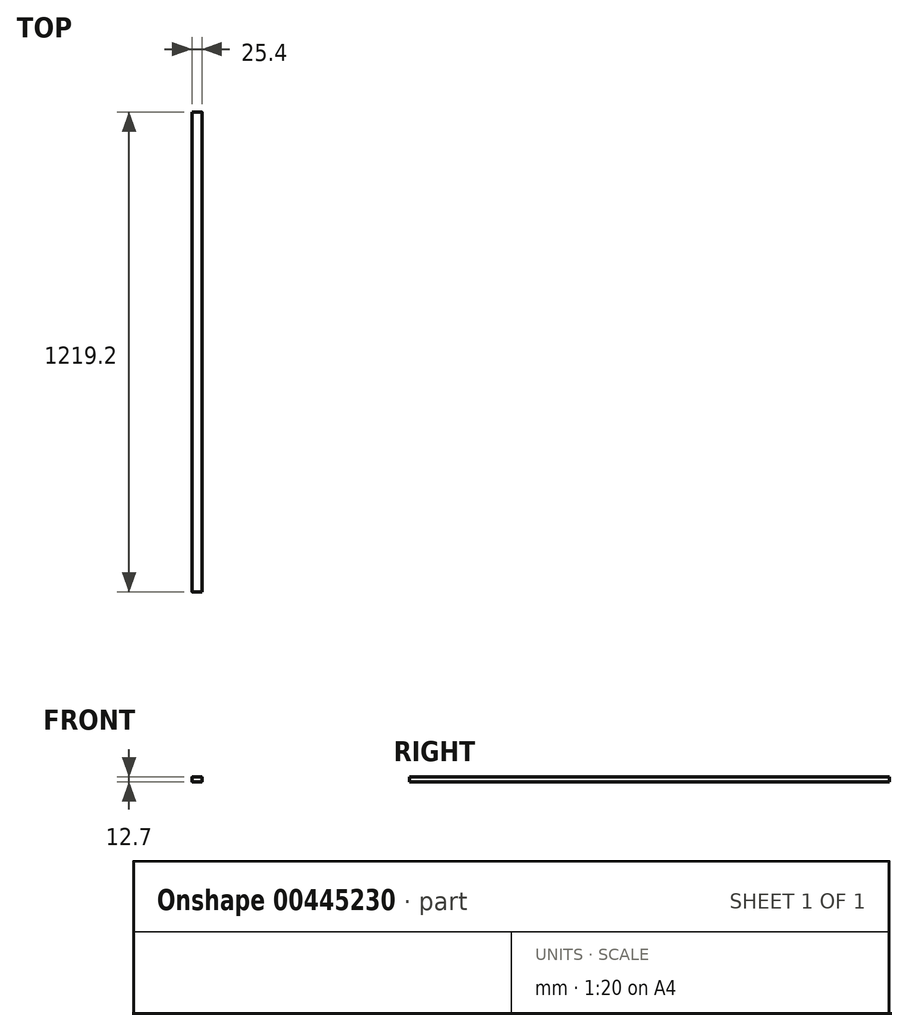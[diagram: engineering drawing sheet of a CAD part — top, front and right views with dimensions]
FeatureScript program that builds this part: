
annotation { "Feature Type Name" : "Feature", "Feature Type Description" : "" }
export const myFeature = defineFeature(function(context is Context, id is Id, definition is map)
    precondition{}
    {
        {
            var Q0;
            Q0=qCreatedBy(makeId("Front.planeOp"),FACE);
            var sketch = newSketch(context, id + "F0", { "sketchPlane" : qUnion([Q0])});
            skLineSegment(sketch, "E0.bottom", {"start": v(-12.7, 6.35) * mm, "end": v(12.7, 6.35) * mm});
            skLineSegment(sketch, "E0.top", {"start": v(-12.7, -6.35) * mm, "end": v(12.7, -6.35) * mm});
            skLineSegment(sketch, "E0.left", {"start": v(-12.7, 6.35) * mm, "end": v(-12.7, -6.35) * mm});
            skLineSegment(sketch, "E0.right", {"start": v(12.7, 6.35) * mm, "end": v(12.7, -6.35) * mm});
            skPoint(sketch, "E0.middle", {"position": v(0, 0) * mm});
            skSolve(sketch);
        }
        {
            var Q0;
            Q0 = qSketchRegion(id + "F0", true);
            extrude(context, id + "F1", {"entities" : qUnion([Q0]), "oppositeDirection" : true, "depth" : 1219.2 * mm});
        }
        {
            var Q0;
            Q0=makeQuery(id+"F1.opExtrude","SWEPT_EDGE",EDGE,{"disambiguationData":[OSD([sQuery(id+"F0.wireOp",EDGE,"E0.bottom"),sQuery(id+"F0.wireOp",EDGE,"E0.right")])]});
            var Q1;
            Q1=makeQuery(id+"F1.opExtrude","SWEPT_EDGE",EDGE,{"disambiguationData":[OSD([sQuery(id+"F0.wireOp",EDGE,"E0.bottom"),sQuery(id+"F0.wireOp",EDGE,"E0.left")])]});
            var Q2;
            Q2=makeQuery(id+"F1.opExtrude","SWEPT_EDGE",EDGE,{"disambiguationData":[OSD([sQuery(id+"F0.wireOp",EDGE,"E0.top"),sQuery(id+"F0.wireOp",EDGE,"E0.right")])]});
            var Q3;
            Q3=makeQuery(id+"F1.opExtrude","SWEPT_EDGE",EDGE,{"disambiguationData":[OSD([sQuery(id+"F0.wireOp",EDGE,"E0.top"),sQuery(id+"F0.wireOp",EDGE,"E0.left")])]});
            fillet(context, id + "F2", {"entities" : qUnion([Q0, Q1, Q2, Q3]), "radius" : 1 * mm, "tangentPropagation" : true, "allowEdgeOverflow" : false});
        }
    });
